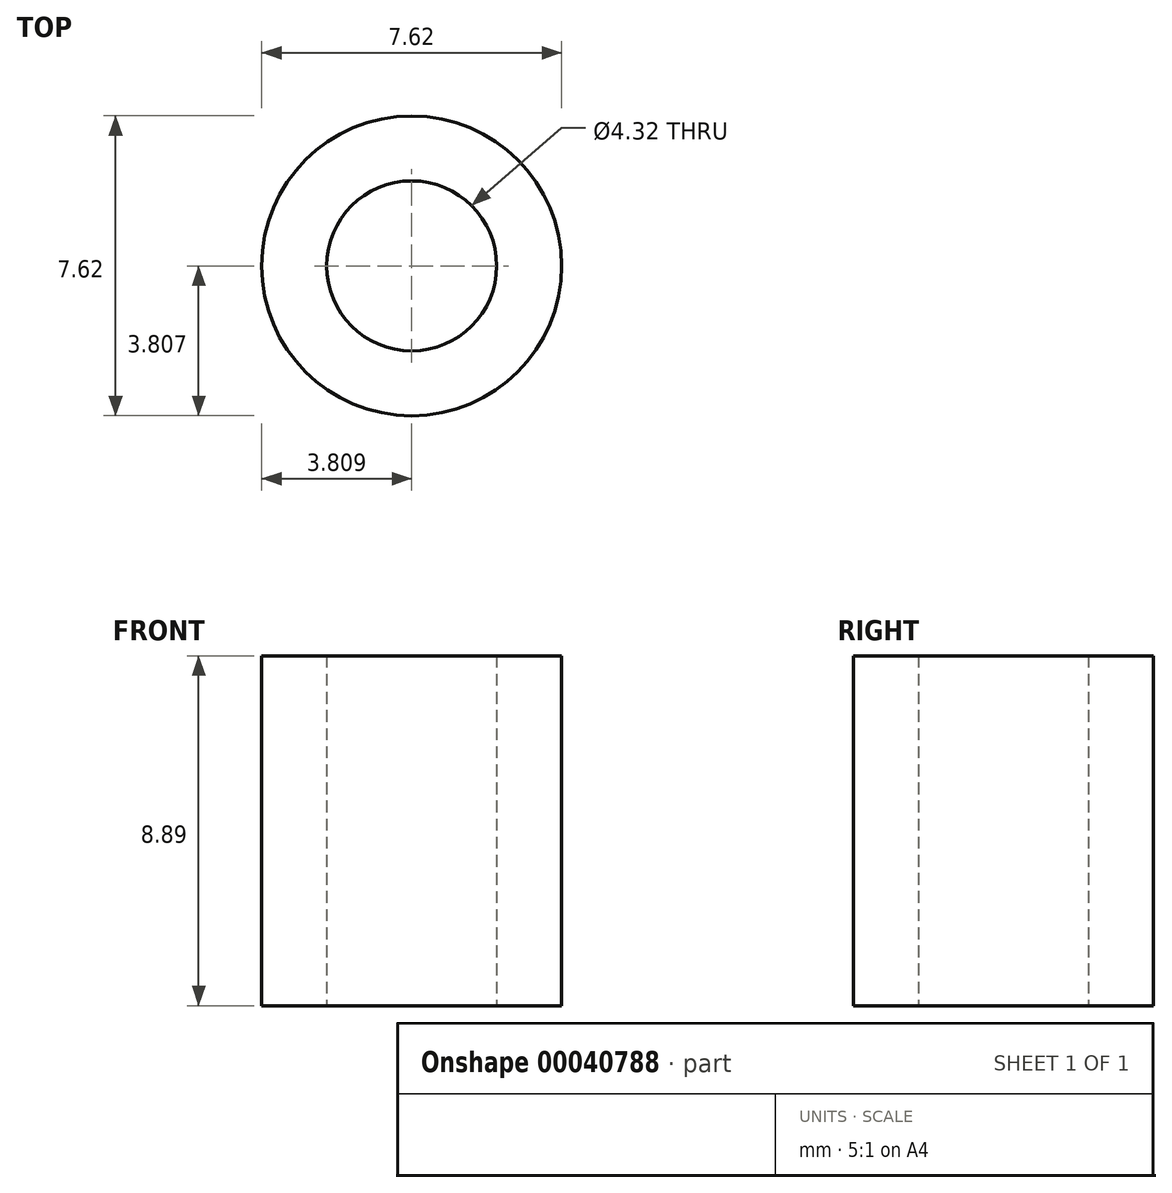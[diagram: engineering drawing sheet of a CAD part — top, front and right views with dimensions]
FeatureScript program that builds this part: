
annotation { "Feature Type Name" : "Feature", "Feature Type Description" : "" }
export const myFeature = defineFeature(function(context is Context, id is Id, definition is map)
    precondition{}
    {
        {
            var Q0;
            Q0=qCreatedBy(makeId("Top.planeOp"),FACE);
            var sketch = newSketch(context, id + "F0", { "sketchPlane" : qUnion([Q0])});
            skCircle(sketch, "E0", {"center": v(-56.98, 45.83) * mm, "radius": 2.16 * mm});
            skCircle(sketch, "E1", {"center": v(-56.98, 45.83) * mm, "radius": 3.81 * mm});
            skSolve(sketch);
        }
        {
            var Q0;
            Q0 = qSketchRegion(id + "F0", true);
            extrude(context, id + "F1", {"entities" : qUnion([Q0]), "depth" : 8.9 * mm});
        }
    });
